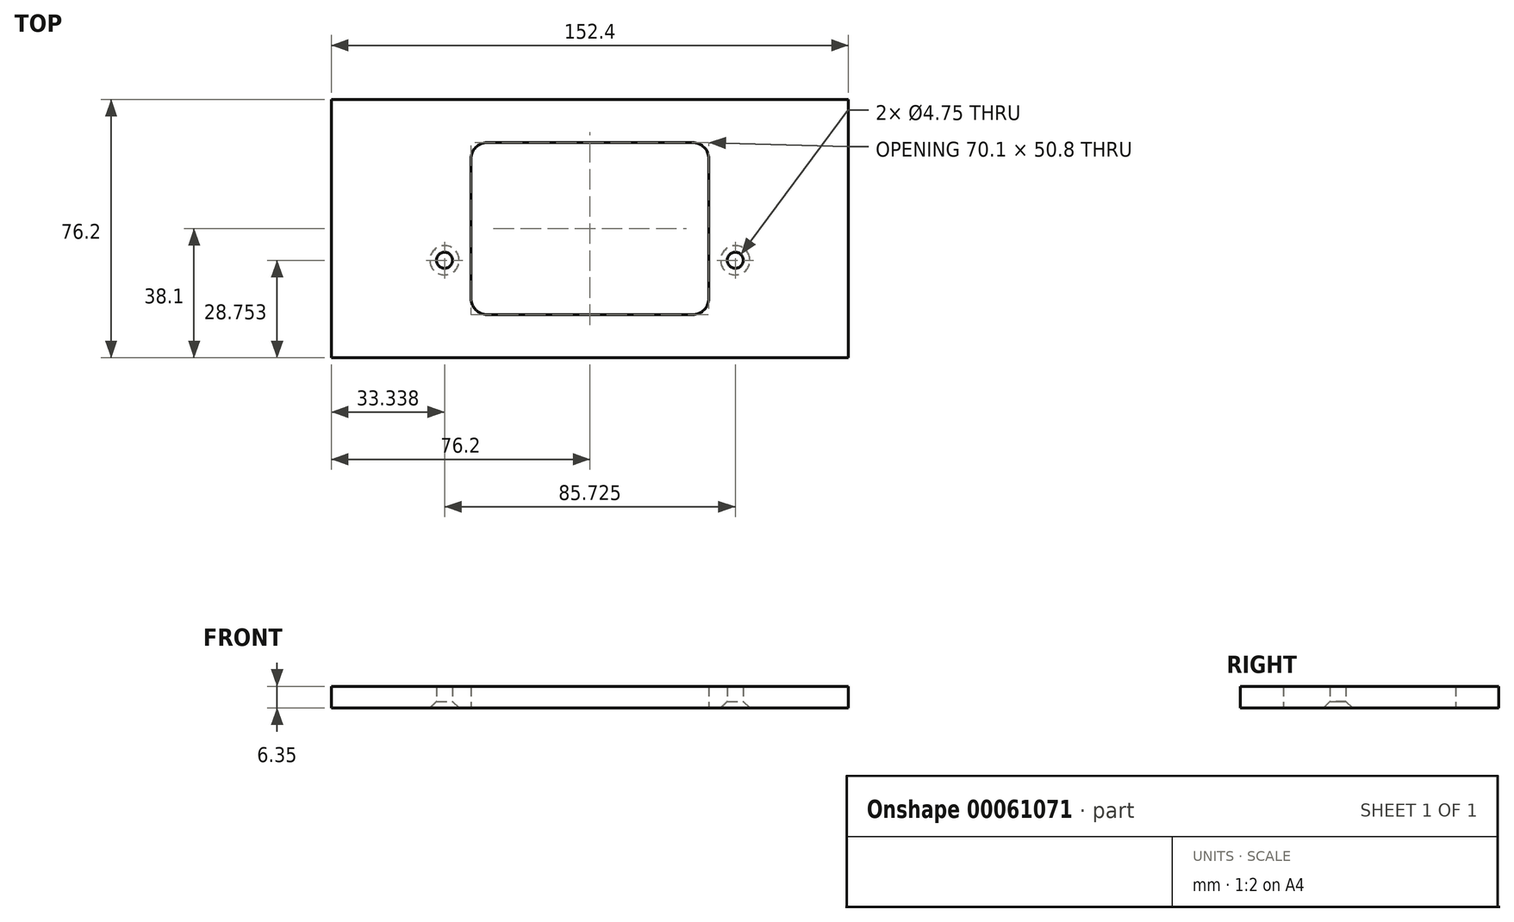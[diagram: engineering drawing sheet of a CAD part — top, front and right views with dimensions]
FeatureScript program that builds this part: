
annotation { "Feature Type Name" : "Feature", "Feature Type Description" : "" }
export const myFeature = defineFeature(function(context is Context, id is Id, definition is map)
    precondition{}
    {
        {
            var Q0;
            Q0=qCreatedBy(makeId("Top.planeOp"),FACE);
            var sketch = newSketch(context, id + "F0", { "sketchPlane" : qUnion([Q0])});
            skLineSegment(sketch, "E0.rect.bottom", {"start": v(-76.2, -38.1) * mm, "end": v(76.2, -38.1) * mm});
            skLineSegment(sketch, "E0.rect.top", {"start": v(-76.2, 38.1) * mm, "end": v(76.2, 38.1) * mm});
            skLineSegment(sketch, "E0.rect.left", {"start": v(-76.2, -38.1) * mm, "end": v(-76.2, 38.1) * mm});
            skLineSegment(sketch, "E0.rect.right", {"start": v(76.2, -38.1) * mm, "end": v(76.2, 38.1) * mm});
            skPoint(sketch, "E0.rect.middle", {"position": v(0, 0) * mm});
            skLineSegment(sketch, "E1.rect.bottom", {"start": v(-30.3, -25.4) * mm, "end": v(30.3, -25.4) * mm});
            skLineSegment(sketch, "E1.rect.top", {"start": v(-30.3, 25.4) * mm, "end": v(30.3, 25.4) * mm});
            skLineSegment(sketch, "E1.rect.left", {"start": v(-35.05, -20.65) * mm, "end": v(-35.05, 20.65) * mm});
            skLineSegment(sketch, "E1.rect.right", {"start": v(35.05, -20.65) * mm, "end": v(35.05, 20.65) * mm});
            skPoint(sketch, "E2", {"position": v(-42.86, -9.35) * mm});
            skPoint(sketch, "E3", {"position": v(42.86, -9.35) * mm});
            skPoint(sketch, "E4.visualSharp", {"position": v(-35.05, 25.4) * mm});
            skArc(sketch, "E4.filletArc", {"start": v(-30.3, 25.4) * mm, "mid": v(-33.66, 24) * mm, "end": v(-35.05, 20.65) * mm});
            skPoint(sketch, "E5.visualSharp", {"position": v(-35.05, -25.4) * mm});
            skArc(sketch, "E5.filletArc", {"start": v(-35.05, -20.65) * mm, "mid": v(-33.66, -24) * mm, "end": v(-30.3, -25.4) * mm});
            skPoint(sketch, "E6.visualSharp", {"position": v(35.05, -25.4) * mm});
            skArc(sketch, "E6.filletArc", {"start": v(30.3, -25.4) * mm, "mid": v(33.66, -24) * mm, "end": v(35.05, -20.65) * mm});
            skPoint(sketch, "E7.visualSharp", {"position": v(35.05, 25.4) * mm});
            skArc(sketch, "E7.filletArc", {"start": v(35.05, 20.65) * mm, "mid": v(33.66, 24) * mm, "end": v(30.3, 25.4) * mm});
            skSolve(sketch);
        }
        {
            var Q0;
            Q0 = qSketchRegion(id + "F0", true);
            extrude(context, id + "F1", {"entities" : qUnion([Q0]), "depth" : 6.35 * mm});
        }
        {
            var Q0;
            Q0=sQuery(id+"F0.wireOp",VERTEX,"E2");
            var Q1;
            Q1=sQuery(id+"F0.wireOp",VERTEX,"E3");
            var Q2;
            Q2=makeQuery(id+"F1.opExtrude","SWEPT_BODY",BODY,{"disambiguationData":[OSD([sQuery(id+"F0.wireOp",EDGE,"E0.rect.bottom"),sQuery(id+"F0.wireOp",EDGE,"E0.rect.top"),sQuery(id+"F0.wireOp",EDGE,"E0.rect.left"),sQuery(id+"F0.wireOp",EDGE,"E0.rect.right"),sQuery(id+"F0.wireOp",EDGE,"E1.rect.bottom"),sQuery(id+"F0.wireOp",EDGE,"E1.rect.top"),sQuery(id+"F0.wireOp",EDGE,"E1.rect.left"),sQuery(id+"F0.wireOp",EDGE,"E1.rect.right"),sQuery(id+"F0.wireOp",EDGE,"E4.filletArc"),sQuery(id+"F0.wireOp",EDGE,"E5.filletArc"),sQuery(id+"F0.wireOp",EDGE,"E6.filletArc"),sQuery(id+"F0.wireOp",EDGE,"E7.filletArc")])]});
            hole(context, id + "F2", {"style" : HoleStyle.C_SINK, "holeDiameter" : 4.75 * mm, "cSinkDiameter" : 8.6 * mm, "endStyle" : HoleEndStyle.THROUGH, "oppositeDirection" : true, "locations" : qUnion([Q0, Q1]), "scope" : qUnion([Q2]), "cSinkAngle" : 90 * degree});
        }
    });
